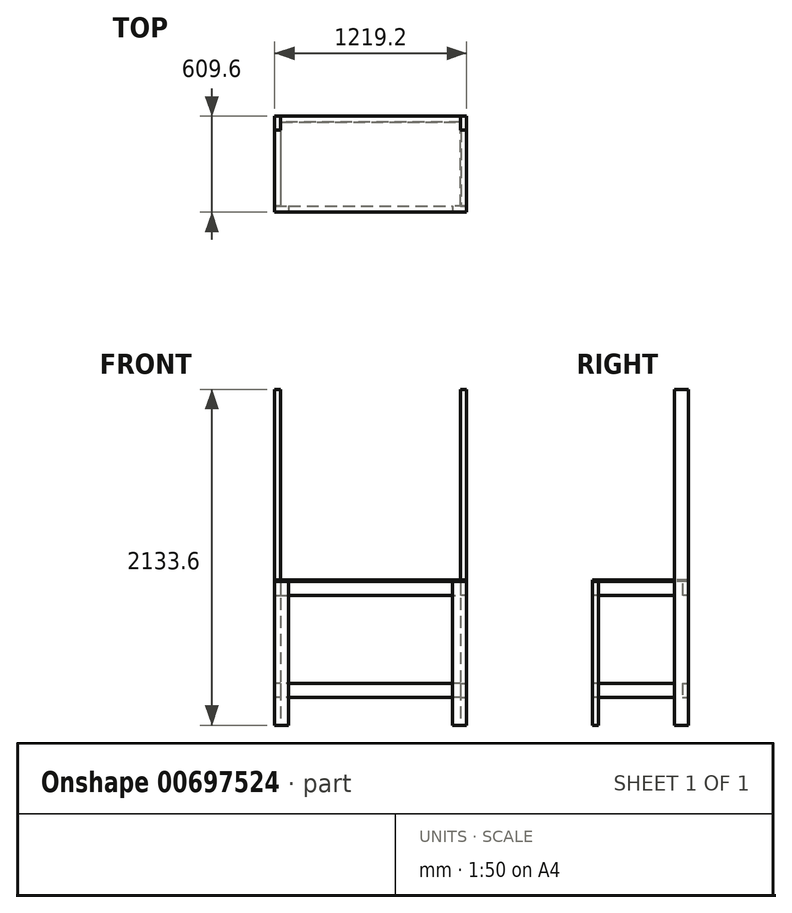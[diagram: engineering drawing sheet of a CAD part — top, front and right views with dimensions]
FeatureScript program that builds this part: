
annotation { "Feature Type Name" : "Feature", "Feature Type Description" : "" }
export const myFeature = defineFeature(function(context is Context, id is Id, definition is map)
    precondition{}
    {
        {
            var Q0;
            Q0=qCreatedBy(makeId("Top.planeOp"),FACE);
            var sketch = newSketch(context, id + "F0", { "sketchPlane" : qUnion([Q0])});
            skLineSegment(sketch, "E0.bottom", {"start": v(-609.6, 304.8) * mm, "end": v(609.6, 304.8) * mm, "construction": true});
            skLineSegment(sketch, "E0.top", {"start": v(-609.6, -304.8) * mm, "end": v(609.6, -304.8) * mm, "construction": true});
            skLineSegment(sketch, "E0.left", {"start": v(-609.6, 304.8) * mm, "end": v(-609.6, -304.8) * mm, "construction": true});
            skLineSegment(sketch, "E0.right", {"start": v(609.6, 304.8) * mm, "end": v(609.6, -304.8) * mm, "construction": true});
            skLineSegment(sketch, "E1.bottom", {"start": v(-609.6, 304.8) * mm, "end": v(-571.5, 304.8) * mm});
            skLineSegment(sketch, "E1.top", {"start": v(-609.6, 215.9) * mm, "end": v(-571.5, 215.9) * mm});
            skLineSegment(sketch, "E1.left", {"start": v(-609.6, 304.8) * mm, "end": v(-609.6, 215.9) * mm});
            skLineSegment(sketch, "E1.right", {"start": v(-571.5, 304.8) * mm, "end": v(-571.5, 215.9) * mm});
            skLineSegment(sketch, "E2.bottom", {"start": v(609.6, 304.8) * mm, "end": v(571.5, 304.8) * mm});
            skLineSegment(sketch, "E2.top", {"start": v(609.6, 215.9) * mm, "end": v(571.5, 215.9) * mm});
            skLineSegment(sketch, "E2.left", {"start": v(609.6, 304.8) * mm, "end": v(609.6, 215.9) * mm});
            skLineSegment(sketch, "E2.right", {"start": v(571.5, 304.8) * mm, "end": v(571.5, 215.9) * mm});
            skLineSegment(sketch, "E3.bottom", {"start": v(609.6, -304.8) * mm, "end": v(520.7, -304.8) * mm});
            skLineSegment(sketch, "E3.top", {"start": v(609.6, -266.7) * mm, "end": v(520.7, -266.7) * mm});
            skLineSegment(sketch, "E3.left", {"start": v(609.6, -304.8) * mm, "end": v(609.6, -266.7) * mm});
            skLineSegment(sketch, "E3.right", {"start": v(520.7, -304.8) * mm, "end": v(520.7, -266.7) * mm});
            skLineSegment(sketch, "E4.bottom", {"start": v(-609.6, -304.8) * mm, "end": v(-520.7, -304.8) * mm});
            skLineSegment(sketch, "E4.top", {"start": v(-609.6, -266.7) * mm, "end": v(-520.7, -266.7) * mm});
            skLineSegment(sketch, "E4.left", {"start": v(-609.6, -304.8) * mm, "end": v(-609.6, -266.7) * mm});
            skLineSegment(sketch, "E4.right", {"start": v(-520.7, -304.8) * mm, "end": v(-520.7, -266.7) * mm});
            skSolve(sketch);
        }
        {
            var Q0;
            Q0=makeQuery(id+"F0.imprint","IMPRINT",FACE,{"disambiguationData":[TD([[makeQuery(id+"F0.imprint","IMPRINT",EDGE,{"derivedFrom":sQuery(id+"F0.wireOp",EDGE,"E1.bottom")}),-1.0]])]});
            var Q1;
            Q1=makeQuery(id+"F0.imprint","IMPRINT",FACE,{"disambiguationData":[TD([[makeQuery(id+"F0.imprint","IMPRINT",EDGE,{"derivedFrom":sQuery(id+"F0.wireOp",EDGE,"E2.bottom")}),1.0]])]});
            extrude(context, id + "F1", {"entities" : qUnion([Q0, Q1]), "depth" : 2133.6 * mm});
        }
        {
            var Q0;
            Q0=makeQuery(id+"F0.imprint","IMPRINT",FACE,{"disambiguationData":[TD([[makeQuery(id+"F0.imprint","IMPRINT",EDGE,{"derivedFrom":sQuery(id+"F0.wireOp",EDGE,"E4.bottom")}),1.0]])]});
            var Q1;
            Q1=makeQuery(id+"F0.imprint","IMPRINT",FACE,{"disambiguationData":[TD([[makeQuery(id+"F0.imprint","IMPRINT",EDGE,{"derivedFrom":sQuery(id+"F0.wireOp",EDGE,"E3.bottom")}),-1.0]])]});
            extrude(context, id + "F2", {"entities" : qUnion([Q0, Q1]), "depth" : 914.4 * mm});
        }
        {
            var Q0;
            Q0=makeQuery(id+"F2.opExtrude","SWEPT_FACE",FACE,{"disambiguationData":[OSD([sQuery(id+"F0.wireOp",EDGE,"E4.bottom")])]});
            var sketch = newSketch(context, id + "F3", { "sketchPlane" : qUnion([Q0])});
            skLineSegment(sketch, "E5.bottom", {"start": v(-609.6, 0) * mm, "end": v(602.1, 0) * mm, "construction": true});
            skLineSegment(sketch, "E5.top", {"start": v(-609.6, 177.8) * mm, "end": v(602.1, 177.8) * mm, "construction": true});
            skLineSegment(sketch, "E5.left", {"start": v(-609.6, 0) * mm, "end": v(-609.6, 177.8) * mm, "construction": true});
            skLineSegment(sketch, "E5.right", {"start": v(602.1, 0) * mm, "end": v(602.1, 177.8) * mm, "construction": true});
            skLineSegment(sketch, "E6.bottom", {"start": v(-520.7, 177.8) * mm, "end": v(520.7, 177.8) * mm});
            skLineSegment(sketch, "E6.top", {"start": v(-520.7, 266.7) * mm, "end": v(520.7, 266.7) * mm});
            skLineSegment(sketch, "E6.left", {"start": v(-520.7, 177.8) * mm, "end": v(-520.7, 266.7) * mm});
            skLineSegment(sketch, "E6.right", {"start": v(520.7, 177.8) * mm, "end": v(520.7, 266.7) * mm});
            skSolve(sketch);
        }
        {
            var Q0;
            Q0=makeQuery(id+"F3.imprint","IMPRINT",FACE,{"disambiguationData":[TD([[makeQuery(id+"F3.imprint","IMPRINT",EDGE,{"derivedFrom":sQuery(id+"F3.wireOp",EDGE,"E6.bottom")}),1.0]])]});
            extrude(context, id + "F4", {"entities" : qUnion([Q0]), "oppositeDirection" : true, "depth" : 38.1 * mm});
        }
        {
            var Q0;
            Q0=makeQuery(id+"F2.opExtrude","SWEPT_FACE",FACE,{"disambiguationData":[OSD([sQuery(id+"F0.wireOp",EDGE,"E3.left")])]});
            var sketch = newSketch(context, id + "F5", { "sketchPlane" : qUnion([Q0])});
            skLineSegment(sketch, "E7.bottom", {"start": v(-304.8, 0) * mm, "end": v(553.73, 0) * mm, "construction": true});
            skLineSegment(sketch, "E7.top", {"start": v(-304.8, 177.8) * mm, "end": v(553.73, 177.8) * mm, "construction": true});
            skLineSegment(sketch, "E7.left", {"start": v(-304.8, 0) * mm, "end": v(-304.8, 177.8) * mm, "construction": true});
            skLineSegment(sketch, "E7.right", {"start": v(553.73, 0) * mm, "end": v(553.73, 177.8) * mm, "construction": true});
            skLineSegment(sketch, "E8.bottom", {"start": v(-266.7, 177.8) * mm, "end": v(215.9, 177.8) * mm});
            skLineSegment(sketch, "E8.top", {"start": v(-266.7, 266.7) * mm, "end": v(215.9, 266.7) * mm});
            skLineSegment(sketch, "E8.left", {"start": v(-266.7, 177.8) * mm, "end": v(-266.7, 266.7) * mm});
            skLineSegment(sketch, "E8.right", {"start": v(215.9, 177.8) * mm, "end": v(215.9, 266.7) * mm});
            skSolve(sketch);
        }
        {
            var Q0;
            Q0=makeQuery(id+"F5.imprint","IMPRINT",FACE,{"disambiguationData":[TD([[makeQuery(id+"F5.imprint","IMPRINT",EDGE,{"derivedFrom":sQuery(id+"F5.wireOp",EDGE,"E8.bottom")}),1.0]])]});
            extrude(context, id + "F6", {"entities" : qUnion([Q0]), "oppositeDirection" : true, "depth" : 38.1 * mm});
        }
        {
            var Q0;
            Q0=makeQuery(id+"F1.opExtrude","SWEPT_FACE",FACE,{"disambiguationData":[OSD([sQuery(id+"F0.wireOp",EDGE,"E2.bottom")])]});
            var sketch = newSketch(context, id + "F7", { "sketchPlane" : qUnion([Q0])});
            skLineSegment(sketch, "E9.bottom", {"start": v(-609.6, 0) * mm, "end": v(676.26, 0) * mm, "construction": true});
            skLineSegment(sketch, "E9.top", {"start": v(-609.6, 177.8) * mm, "end": v(676.26, 177.8) * mm, "construction": true});
            skLineSegment(sketch, "E9.left", {"start": v(-609.6, 0) * mm, "end": v(-609.6, 177.8) * mm, "construction": true});
            skLineSegment(sketch, "E9.right", {"start": v(676.26, 0) * mm, "end": v(676.26, 177.8) * mm, "construction": true});
            skLineSegment(sketch, "E10.bottom", {"start": v(-571.5, 177.8) * mm, "end": v(571.5, 177.8) * mm});
            skLineSegment(sketch, "E10.top", {"start": v(-571.5, 266.7) * mm, "end": v(571.5, 266.7) * mm});
            skLineSegment(sketch, "E10.left", {"start": v(-571.5, 177.8) * mm, "end": v(-571.5, 266.7) * mm});
            skLineSegment(sketch, "E10.right", {"start": v(571.5, 177.8) * mm, "end": v(571.5, 266.7) * mm});
            skSolve(sketch);
        }
        {
            var Q0;
            Q0=qSketchRegion(id+"F7",true);
            extrude(context, id + "F8", {"entities" : qUnion([Q0]), "oppositeDirection" : true, "depth" : 38.1 * mm});
        }
        {
            var Q0;
            Q0=makeQuery(id+"F1.opExtrude","SWEPT_FACE",FACE,{"disambiguationData":[OSD([sQuery(id+"F0.wireOp",EDGE,"E1.left")])]});
            var sketch = newSketch(context, id + "F9", { "sketchPlane" : qUnion([Q0])});
            skLineSegment(sketch, "E11.bottom", {"start": v(-304.8, 0) * mm, "end": v(286.26, 0) * mm, "construction": true});
            skLineSegment(sketch, "E11.top", {"start": v(-304.8, 177.8) * mm, "end": v(286.26, 177.8) * mm, "construction": true});
            skLineSegment(sketch, "E11.left", {"start": v(-304.8, 0) * mm, "end": v(-304.8, 177.8) * mm, "construction": true});
            skLineSegment(sketch, "E11.right", {"start": v(286.26, 0) * mm, "end": v(286.26, 177.8) * mm, "construction": true});
            skLineSegment(sketch, "E12.bottom", {"start": v(-215.9, 177.8) * mm, "end": v(266.7, 177.8) * mm});
            skLineSegment(sketch, "E12.top", {"start": v(-215.9, 266.7) * mm, "end": v(266.7, 266.7) * mm});
            skLineSegment(sketch, "E12.left", {"start": v(-215.9, 177.8) * mm, "end": v(-215.9, 266.7) * mm});
            skLineSegment(sketch, "E12.right", {"start": v(266.7, 177.8) * mm, "end": v(266.7, 266.7) * mm});
            skSolve(sketch);
        }
        {
            var Q0;
            Q0=makeQuery(id+"F9.imprint","IMPRINT",FACE,{"disambiguationData":[TD([[makeQuery(id+"F9.imprint","IMPRINT",EDGE,{"derivedFrom":sQuery(id+"F9.wireOp",EDGE,"E12.bottom")}),1.0]])]});
            extrude(context, id + "F10", {"entities" : qUnion([Q0]), "oppositeDirection" : true, "depth" : 38.1 * mm});
        }
        {
            var Q0;
            Q0=makeQuery(id+"F2.opExtrude","CAP_FACE",FACE,{"disambiguationData":[OSD([sQuery(id+"F0.wireOp",EDGE,"E4.bottom"),sQuery(id+"F0.wireOp",EDGE,"E4.top"),sQuery(id+"F0.wireOp",EDGE,"E4.left"),sQuery(id+"F0.wireOp",EDGE,"E4.right")])],"isStart":false});
            var sketch = newSketch(context, id + "F11", { "sketchPlane" : qUnion([Q0])});
            skLineSegment(sketch, "E13.bottom", {"start": v(-609.6, -304.8) * mm, "end": v(609.6, -304.8) * mm, "construction": true});
            skLineSegment(sketch, "E13.top", {"start": v(-609.6, 304.8) * mm, "end": v(609.6, 304.8) * mm, "construction": true});
            skLineSegment(sketch, "E13.left", {"start": v(-609.6, -304.8) * mm, "end": v(-609.6, 304.8) * mm, "construction": true});
            skLineSegment(sketch, "E13.right", {"start": v(609.6, -304.8) * mm, "end": v(609.6, 304.8) * mm, "construction": true});
            skLineSegment(sketch, "E14.bottom", {"start": v(-609.6, -266.7) * mm, "end": v(-570.84, -266.7) * mm});
            skLineSegment(sketch, "E14.top", {"start": v(-609.6, 215.9) * mm, "end": v(-570.84, 215.9) * mm});
            skLineSegment(sketch, "E14.left", {"start": v(-609.6, -266.7) * mm, "end": v(-609.6, 215.9) * mm});
            skLineSegment(sketch, "E14.right", {"start": v(-570.84, -266.7) * mm, "end": v(-570.84, 215.9) * mm});
            skLineSegment(sketch, "E15.bottom", {"start": v(-570.84, 304.8) * mm, "end": v(572.16, 304.8) * mm});
            skLineSegment(sketch, "E15.top", {"start": v(-570.84, 267.05) * mm, "end": v(572.16, 267.05) * mm});
            skLineSegment(sketch, "E15.left", {"start": v(-570.84, 304.8) * mm, "end": v(-570.84, 267.05) * mm});
            skLineSegment(sketch, "E15.right", {"start": v(572.16, 304.8) * mm, "end": v(572.16, 267.05) * mm});
            skLineSegment(sketch, "E16.bottom", {"start": v(609.6, 215.9) * mm, "end": v(572.16, 215.9) * mm});
            skLineSegment(sketch, "E16.top", {"start": v(609.6, -266.7) * mm, "end": v(572.16, -266.7) * mm});
            skLineSegment(sketch, "E16.left", {"start": v(609.6, 215.9) * mm, "end": v(609.6, -266.7) * mm});
            skLineSegment(sketch, "E16.right", {"start": v(572.16, 215.9) * mm, "end": v(572.16, -266.7) * mm});
            skLineSegment(sketch, "E17.bottom", {"start": v(520.7, -266.7) * mm, "end": v(-520.7, -266.7) * mm});
            skLineSegment(sketch, "E17.top", {"start": v(520.7, -304.8) * mm, "end": v(-520.7, -304.8) * mm});
            skLineSegment(sketch, "E17.left", {"start": v(520.7, -266.7) * mm, "end": v(520.7, -304.8) * mm});
            skLineSegment(sketch, "E17.right", {"start": v(-520.7, -266.7) * mm, "end": v(-520.7, -304.8) * mm});
            skSolve(sketch);
        }
        {
            var Q0;
            Q0=qSketchRegion(id+"F11",true);
            extrude(context, id + "F12", {"entities" : qUnion([Q0]), "oppositeDirection" : true, "depth" : 88.9 * mm});
        }
        {
            var Q0;
            Q0=makeQuery(id+"F2.opExtrude","CAP_FACE",FACE,{"disambiguationData":[OSD([sQuery(id+"F0.wireOp",EDGE,"E4.bottom"),sQuery(id+"F0.wireOp",EDGE,"E4.top"),sQuery(id+"F0.wireOp",EDGE,"E4.left"),sQuery(id+"F0.wireOp",EDGE,"E4.right")])],"isStart":false});
            var sketch = newSketch(context, id + "F13", { "sketchPlane" : qUnion([Q0])});
            skLineSegment(sketch, "E18", {"start": v(-609.6, -304.8) * mm, "end": v(-609.6, 215.9) * mm, "construction": true});
            skLineSegment(sketch, "E19", {"start": v(-609.6, 215.9) * mm, "end": v(-571.5, 215.9) * mm});
            skLineSegment(sketch, "E20", {"start": v(-571.5, 215.9) * mm, "end": v(-571.5, 304.8) * mm});
            skLineSegment(sketch, "E21", {"start": v(-571.5, 304.8) * mm, "end": v(571.5, 304.8) * mm});
            skLineSegment(sketch, "E22", {"start": v(571.5, 304.8) * mm, "end": v(571.5, 215.9) * mm});
            skLineSegment(sketch, "E23", {"start": v(571.5, 215.9) * mm, "end": v(609.6, 215.9) * mm});
            skLineSegment(sketch, "E24", {"start": v(609.6, 215.9) * mm, "end": v(609.6, -304.8) * mm});
            skLineSegment(sketch, "E25", {"start": v(609.6, -304.8) * mm, "end": v(-609.6, -304.8) * mm});
            skLineSegment(sketch, "E26", {"start": v(-609.6, 215.9) * mm, "end": v(-609.6, -304.8) * mm});
            skSolve(sketch);
        }
        {
            var Q0;
            Q0=qSketchRegion(id+"F13",true);
            extrude(context, id + "F14", {"entities" : qUnion([Q0]), "depth" : 9.52 * mm});
        }
    });
